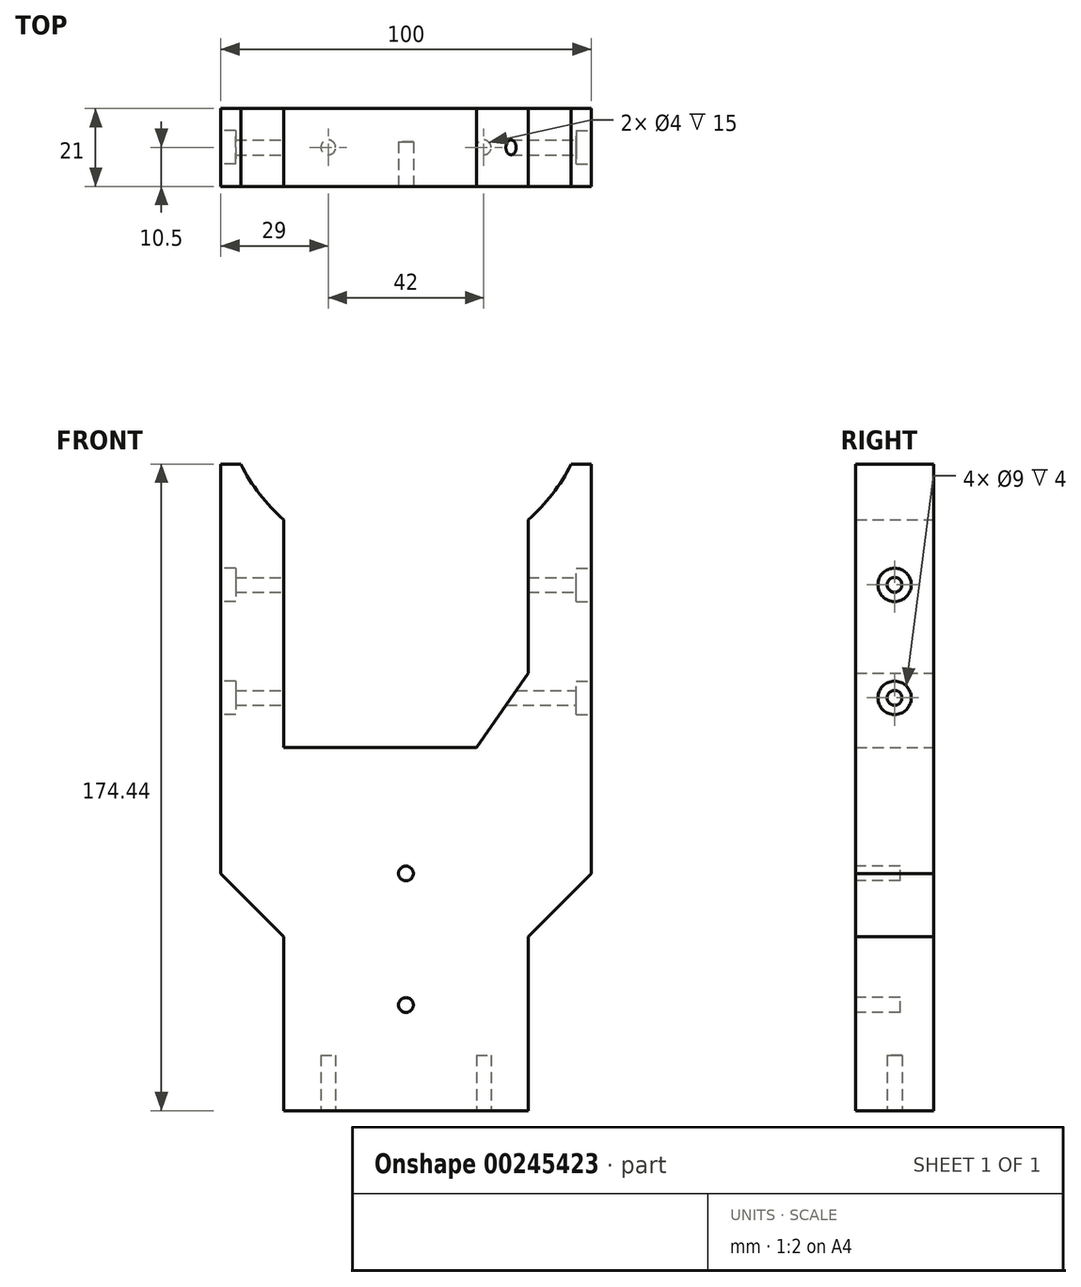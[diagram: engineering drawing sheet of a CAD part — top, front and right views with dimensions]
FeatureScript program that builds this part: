
annotation { "Feature Type Name" : "Feature", "Feature Type Description" : "" }
export const myFeature = defineFeature(function(context is Context, id is Id, definition is map)
    precondition{}
    {
        {
            var Q0;
            Q0=qCreatedBy(makeId("Front.planeOp"),FACE);
            var sketch = newSketch(context, id + "F0", { "sketchPlane" : qUnion([Q0])});
            skArc(sketch, "E0", {"start": v(33, -37.56) * mm, "mid": v(39.53, -30.62) * mm, "end": v(44.62, -22.56) * mm});
            skLineSegment(sketch, "E1.left", {"start": v(-50, -22.56) * mm, "end": v(-50, -133) * mm});
            skLineSegment(sketch, "E1.right", {"start": v(50, -22.56) * mm, "end": v(50, -133) * mm});
            skLineSegment(sketch, "E2", {"start": v(0, -99) * mm, "end": v(-33, -99) * mm});
            skLineSegment(sketch, "E3", {"start": v(33, -79) * mm, "end": v(19, -99) * mm});
            skLineSegment(sketch, "E4", {"start": v(0, -99) * mm, "end": v(19, -99) * mm});
            skLineSegment(sketch, "E5", {"start": v(-44.62, -22.56) * mm, "end": v(-50, -22.56) * mm});
            skArc(sketch, "E6.trimOffspring", {"start": v(-44.62, -22.56) * mm, "mid": v(-39.53, -30.62) * mm, "end": v(-33, -37.56) * mm});
            skLineSegment(sketch, "E7.trimOffspring", {"start": v(44.62, -22.56) * mm, "end": v(50, -22.56) * mm});
            skLineSegment(sketch, "E8.trimOffspring", {"start": v(33, -37.56) * mm, "end": v(33, -79) * mm});
            skLineSegment(sketch, "E9.trimOffspring", {"start": v(-33, -37.56) * mm, "end": v(-33, -99) * mm});
            skLineSegment(sketch, "E10.right", {"start": v(33, -150) * mm, "end": v(33, -180) * mm});
            skLineSegment(sketch, "E11.MirrorCS", {"start": v(-33, -150) * mm, "end": v(-33, -180) * mm});
            skLineSegment(sketch, "E12.MirrorCS", {"start": v(0, -197) * mm, "end": v(-33, -197) * mm});
            skLineSegment(sketch, "E13", {"start": v(33, -150) * mm, "end": v(50, -133) * mm});
            skLineSegment(sketch, "E14.MirrorCS", {"start": v(-33, -150) * mm, "end": v(-50, -133) * mm});
            skLineSegment(sketch, "E15", {"start": v(-33, -180) * mm, "end": v(-33, -197) * mm});
            skLineSegment(sketch, "E16", {"start": v(0, -197) * mm, "end": v(33, -197) * mm});
            skLineSegment(sketch, "E17", {"start": v(33, -197) * mm, "end": v(33, -180) * mm});
            skSolve(sketch);
        }
        {
            var Q0;
            Q0=qSketchRegion(id+"F0",true);
            extrude(context, id + "F1", {"entities" : qUnion([Q0]), "depth" : 21 * mm});
        }
        {
            var Q0;
            Q0=qCreatedBy(makeId("Right.planeOp"),FACE);
            var sketch = newSketch(context, id + "F2", { "sketchPlane" : qUnion([Q0])});
            skLineSegment(sketch, "E18", {"start": v(0, 0) * mm, "end": v(0, -42.6) * mm});
            skLineSegment(sketch, "E19", {"start": v(0, -42.6) * mm, "end": v(0, -67.6) * mm});
            skPoint(sketch, "E20.endSnap0", {"position": v(0, -55.1) * mm});
            skCircle(sketch, "E21", {"center": v(-10.5, -55.1) * mm, "radius": 2 * mm});
            skLineSegment(sketch, "E22", {"start": v(0, -67.6) * mm, "end": v(0, -85.6) * mm});
            skCircle(sketch, "E23", {"center": v(-10.5, -85.6) * mm, "radius": 2 * mm});
            skSolve(sketch);
        }
        {
            var Q0;
            Q0=qSketchRegion(id+"F2",true);
            extrude(context, id + "F3", {"entities" : qUnion([Q0]), "operationType" : NewBodyOperationType.REMOVE, "endBound" : BoundingType.SYMMETRIC, "oppositeDirection" : true, "depth" : 100 * mm});
        }
        {
            var Q0;
            Q0=makeQuery(id+"F1.opExtrude","SWEPT_FACE",FACE,{"disambiguationData":[OSD([sQuery(id+"F0.wireOp",EDGE,"E1.left")])]});
            var sketch = newSketch(context, id + "F4", { "sketchPlane" : qUnion([Q0])});
            skCircle(sketch, "E24", {"center": v(10.5, -55.1) * mm, "radius": 4.5 * mm});
            skCircle(sketch, "E25", {"center": v(10.5, -85.6) * mm, "radius": 4.5 * mm});
            skSolve(sketch);
        }
        {
            var Q0;
            Q0=qSketchRegion(id+"F4",true);
            extrude(context, id + "F5", {"entities" : qUnion([Q0]), "operationType" : NewBodyOperationType.REMOVE, "oppositeDirection" : true, "depth" : 4 * mm});
        }
        {
            var Q0;
            Q0=makeQuery(id+"F1.opExtrude","SWEPT_FACE",FACE,{"disambiguationData":[OSD([sQuery(id+"F0.wireOp",EDGE,"E1.right")])]});
            var sketch = newSketch(context, id + "F6", { "sketchPlane" : qUnion([Q0])});
            skCircle(sketch, "E26", {"center": v(-10.5, -55.1) * mm, "radius": 4.5 * mm});
            skCircle(sketch, "E27", {"center": v(-10.5, -85.6) * mm, "radius": 4.5 * mm});
            skSolve(sketch);
        }
        {
            var Q0;
            Q0=qSketchRegion(id+"F6",true);
            extrude(context, id + "F7", {"entities" : qUnion([Q0]), "operationType" : NewBodyOperationType.REMOVE, "oppositeDirection" : true, "depth" : 4 * mm});
        }
        {
            var Q0;
            Q0=makeQuery(id+"F1.opExtrude","SWEPT_FACE",FACE,{"disambiguationData":[OSD([sQuery(id+"F0.wireOp",EDGE,"E12.MirrorCS"),sQuery(id+"F0.wireOp",EDGE,"E16")])]});
            var sketch = newSketch(context, id + "F8", { "sketchPlane" : qUnion([Q0])});
            skLineSegment(sketch, "E28", {"start": v(-33, 10.5) * mm, "end": v(-21, 10.5) * mm});
            skLineSegment(sketch, "E29", {"start": v(33, 10.5) * mm, "end": v(21, 10.5) * mm});
            skCircle(sketch, "E30", {"center": v(-21, 10.5) * mm, "radius": 2 * mm});
            skCircle(sketch, "E31", {"center": v(21, 10.5) * mm, "radius": 2 * mm});
            skSolve(sketch);
        }
        {
            var Q0;
            Q0=qSketchRegion(id+"F8",true);
            extrude(context, id + "F9", {"entities" : qUnion([Q0]), "operationType" : NewBodyOperationType.REMOVE, "oppositeDirection" : true, "depth" : 15 * mm});
        }
        {
            var Q0;
            Q0=makeQuery(id+"F1.opExtrude","CAP_FACE",FACE,{"disambiguationData":[OSD([sQuery(id+"F0.wireOp",EDGE,"E0"),sQuery(id+"F0.wireOp",EDGE,"E1.left"),sQuery(id+"F0.wireOp",EDGE,"E1.right"),sQuery(id+"F0.wireOp",EDGE,"E2"),sQuery(id+"F0.wireOp",EDGE,"E3"),sQuery(id+"F0.wireOp",EDGE,"E4"),sQuery(id+"F0.wireOp",EDGE,"E5"),sQuery(id+"F0.wireOp",EDGE,"E6.trimOffspring"),sQuery(id+"F0.wireOp",EDGE,"E7.trimOffspring"),sQuery(id+"F0.wireOp",EDGE,"E8.trimOffspring"),sQuery(id+"F0.wireOp",EDGE,"E9.trimOffspring"),sQuery(id+"F0.wireOp",EDGE,"E10.right"),sQuery(id+"F0.wireOp",EDGE,"E11.MirrorCS"),sQuery(id+"F0.wireOp",EDGE,"E12.MirrorCS"),sQuery(id+"F0.wireOp",EDGE,"E13"),sQuery(id+"F0.wireOp",EDGE,"E14.MirrorCS"),sQuery(id+"F0.wireOp",EDGE,"E15"),sQuery(id+"F0.wireOp",EDGE,"E16"),sQuery(id+"F0.wireOp",EDGE,"E17")])],"isStart":false});
            var sketch = newSketch(context, id + "F10", { "sketchPlane" : qUnion([Q0])});
            skLineSegment(sketch, "E32", {"start": v(0, -197) * mm, "end": v(0, -140) * mm});
            skPoint(sketch, "E32.endSnap0", {"position": v(0, -197) * mm});
            skLineSegment(sketch, "E33", {"start": v(0, -140) * mm, "end": v(0, -126) * mm});
            skCircle(sketch, "E34", {"center": v(0, -168.5) * mm, "radius": 2 * mm});
            skCircle(sketch, "E35", {"center": v(0, -133) * mm, "radius": 2 * mm});
            skSolve(sketch);
        }
        {
            var Q0;
            Q0=qSketchRegion(id+"F10",true);
            extrude(context, id + "F11", {"entities" : qUnion([Q0]), "operationType" : NewBodyOperationType.REMOVE, "oppositeDirection" : true, "depth" : 12 * mm});
        }
    });
